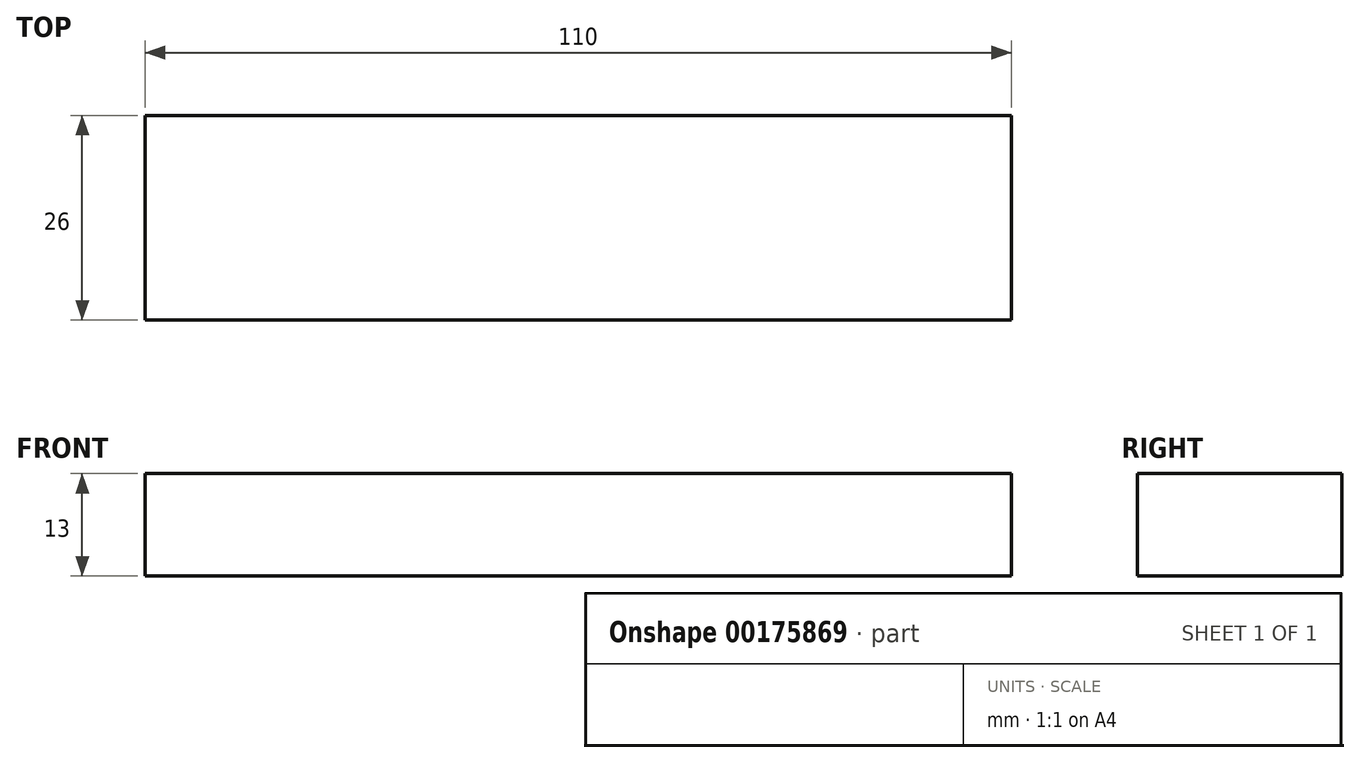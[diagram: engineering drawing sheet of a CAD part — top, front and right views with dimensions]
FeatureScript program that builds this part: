
annotation { "Feature Type Name" : "Feature", "Feature Type Description" : "" }
export const myFeature = defineFeature(function(context is Context, id is Id, definition is map)
    precondition{}
    {
        {
            var Q0;
            Q0=qCreatedBy(makeId("Top.planeOp"),FACE);
            var sketch = newSketch(context, id + "F0", { "sketchPlane" : qUnion([Q0])});
            skLineSegment(sketch, "E0.bottom", {"start": v(-120.49, -9.6) * mm, "end": v(-10.49, -9.6) * mm});
            skLineSegment(sketch, "E0.top", {"start": v(-120.49, -35.6) * mm, "end": v(-10.49, -35.6) * mm});
            skLineSegment(sketch, "E0.left", {"start": v(-120.49, -9.6) * mm, "end": v(-120.49, -35.6) * mm});
            skLineSegment(sketch, "E0.right", {"start": v(-10.49, -9.6) * mm, "end": v(-10.49, -35.6) * mm});
            skSolve(sketch);
        }
        {
            var Q0;
            Q0=qSketchRegion(id+"F0",true);
            extrude(context, id + "F1", {"entities" : qUnion([Q0]), "depth" : 13 * mm});
        }
    });
